# Revit family: Faucet-Lavatory-KOHLER-COMPOSED-K-73053BR_1
name_source: partatom
category: Plumbing Fixtures
revit_build: Autodesk Revit 2017 (Build: 20160225_1515(x64)
units: mm (PartAtom-declared; Revit-internal decimal feet)

## family parameters
Cut with Voids When Loaded = No
Host = Face
OmniClass Number = 23.31.11.00
OmniClass Title = Faucets
Part Type = Normal
Room Calculation Point = No
Round Connector Dimension = Use Diameter
Shared = No

## types (3) — shared parameters
ADA Compliant = No
Assembly Code = D2010
CW Connection = Yes
Cold Water Inlet = Cold Water Inlet
Date Modified = 07/24/2020
Default Elevation = 36"
Description = Single handle bowl faucet
Drain Included = No
Flow Rate = 0 GPM
HW Connection = Yes
Height = 8 1/2"
Hot Water Inlet = Hot Water Inlet
Length = 7 1/8"
Manufacturer = KOHLER Co.
Master Format 2014 = 22 41 39
Master Format 2014 Name = Residential Faucets, Supplies, and Trim
Material = Premium Metal Construction
Pressure = 0.00 psi
Product Name = COMPOSED
Spout Reach = 7 1/8"
URL = https://la.kohler.com
Vent Connection = No
Waste Connection = No
Waste Water Outlet = Waste Water Outlet
WaterSense Certified = No
Width = 2"

## per-type parameters (varying)
| type | Finish | Model | Type |
| CP-Polished Chrome | Kohler-Metal-CP-Polished_Chrome | K-73053BR-4ND-CP | 1 |
| TT-Titanium Silver | Kohler-Metal-TT-Titanium_Silver | K-73053BR-4ND-TT | 3 |
| RGD-Rose Gold | Kohler-Metal-RGD-Rose_Gold | K-73053BR-4ND-RGD | 2 |

## geometry (parser evidence)
native form markers: Sweep x4
no freeform markers — native parametric forms only
